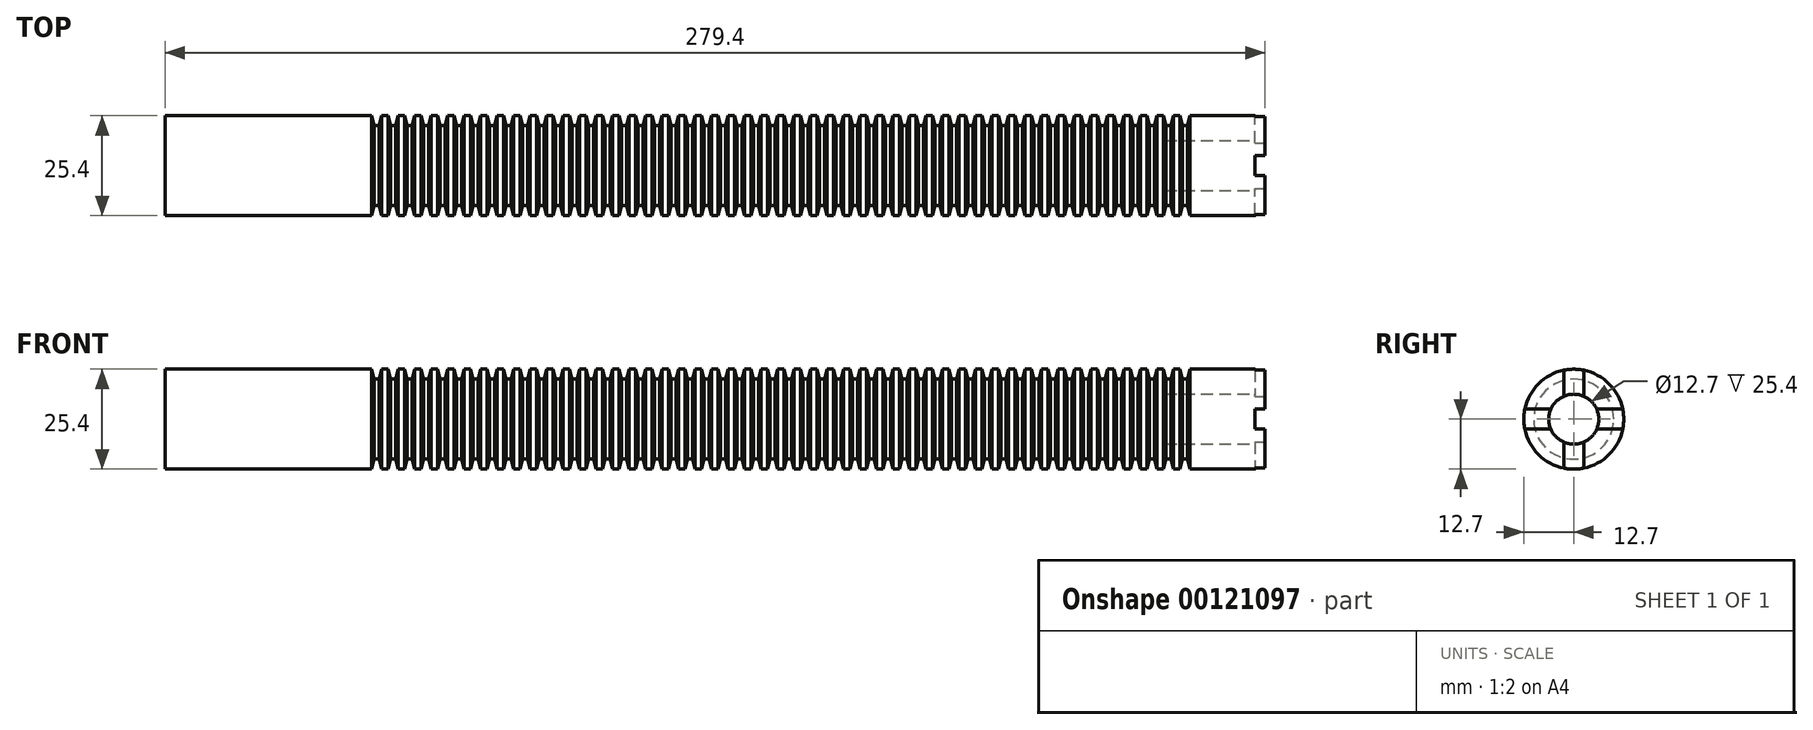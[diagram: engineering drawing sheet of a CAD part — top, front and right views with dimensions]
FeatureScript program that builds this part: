
annotation { "Feature Type Name" : "Feature", "Feature Type Description" : "" }
export const myFeature = defineFeature(function(context is Context, id is Id, definition is map)
    precondition{}
    {
        {
            var Q0;
            Q0=qCreatedBy(makeId("Front.planeOp"),FACE);
            var sketch = newSketch(context, id + "F0", { "sketchPlane" : qUnion([Q0])});
            skLineSegment(sketch, "E0.bottom", {"start": v(0, 0) * mm, "end": v(279.4, 0) * mm});
            skLineSegment(sketch, "E0.top", {"start": v(0, 12.7) * mm, "end": v(52.45, 12.7) * mm});
            skLineSegment(sketch, "E0.left", {"start": v(0, 0) * mm, "end": v(0, 12.7) * mm});
            skLineSegment(sketch, "E0.right", {"start": v(279.4, 0) * mm, "end": v(279.4, 12.7) * mm});
            skLineSegment(sketch, "E1", {"start": v(52.45, 12.7) * mm, "end": v(53.09, 10.16) * mm});
            skLineSegment(sketch, "E2", {"start": v(54.36, 10.16) * mm, "end": v(55, 12.7) * mm});
            skLineSegment(sketch, "E3", {"start": v(53.09, 10.16) * mm, "end": v(54.36, 10.16) * mm});
            skLineSegment(sketch, "E4.trimOffspring", {"start": v(55, 12.7) * mm, "end": v(56.64, 12.7) * mm});
            skLineSegment(sketch, "E5.1.0.0", {"start": v(56.64, 12.7) * mm, "end": v(57.28, 10.16) * mm});
            skLineSegment(sketch, "E5.1.0.1", {"start": v(58.55, 10.16) * mm, "end": v(59.18, 12.7) * mm});
            skLineSegment(sketch, "E5.1.0.2", {"start": v(57.28, 10.16) * mm, "end": v(58.55, 10.16) * mm});
            skLineSegment(sketch, "E5.2.0.0", {"start": v(60.83, 12.7) * mm, "end": v(61.47, 10.16) * mm});
            skLineSegment(sketch, "E5.2.0.1", {"start": v(62.74, 10.16) * mm, "end": v(63.37, 12.7) * mm});
            skLineSegment(sketch, "E5.2.0.2", {"start": v(61.47, 10.16) * mm, "end": v(62.74, 10.16) * mm});
            skLineSegment(sketch, "E5.direction1", {"start": v(55, 12.7) * mm, "end": v(56.64, 12.7) * mm, "construction": true});
            skLineSegment(sketch, "E6.0.3.0", {"start": v(65.02, 12.7) * mm, "end": v(65.66, 10.16) * mm});
            skLineSegment(sketch, "E6.3.3.0", {"start": v(66.93, 10.16) * mm, "end": v(67.56, 12.7) * mm});
            skLineSegment(sketch, "E6.6.3.0", {"start": v(65.66, 10.16) * mm, "end": v(66.93, 10.16) * mm});
            skLineSegment(sketch, "E6.0.4.0", {"start": v(69.21, 12.7) * mm, "end": v(69.85, 10.16) * mm});
            skLineSegment(sketch, "E6.3.4.0", {"start": v(71.12, 10.16) * mm, "end": v(71.75, 12.7) * mm});
            skLineSegment(sketch, "E6.6.4.0", {"start": v(69.85, 10.16) * mm, "end": v(71.12, 10.16) * mm});
            skLineSegment(sketch, "E6.0.5.0", {"start": v(73.4, 12.7) * mm, "end": v(74.04, 10.16) * mm});
            skLineSegment(sketch, "E6.3.5.0", {"start": v(75.31, 10.16) * mm, "end": v(75.95, 12.7) * mm});
            skLineSegment(sketch, "E6.6.5.0", {"start": v(74.04, 10.16) * mm, "end": v(75.31, 10.16) * mm});
            skLineSegment(sketch, "E6.0.6.0", {"start": v(77.6, 12.7) * mm, "end": v(78.23, 10.16) * mm});
            skLineSegment(sketch, "E6.3.6.0", {"start": v(79.5, 10.16) * mm, "end": v(80.14, 12.7) * mm});
            skLineSegment(sketch, "E6.6.6.0", {"start": v(78.23, 10.16) * mm, "end": v(79.5, 10.16) * mm});
            skLineSegment(sketch, "E6.0.7.0", {"start": v(81.79, 12.7) * mm, "end": v(82.42, 10.16) * mm});
            skLineSegment(sketch, "E6.3.7.0", {"start": v(83.7, 10.16) * mm, "end": v(84.33, 12.7) * mm});
            skLineSegment(sketch, "E6.6.7.0", {"start": v(82.42, 10.16) * mm, "end": v(83.7, 10.16) * mm});
            skLineSegment(sketch, "E6.0.8.0", {"start": v(85.98, 12.7) * mm, "end": v(86.61, 10.16) * mm});
            skLineSegment(sketch, "E6.3.8.0", {"start": v(87.88, 10.16) * mm, "end": v(88.52, 12.7) * mm});
            skLineSegment(sketch, "E6.6.8.0", {"start": v(86.61, 10.16) * mm, "end": v(87.88, 10.16) * mm});
            skLineSegment(sketch, "E6.0.9.0", {"start": v(90.17, 12.7) * mm, "end": v(90.8, 10.16) * mm});
            skLineSegment(sketch, "E6.3.9.0", {"start": v(92.07, 10.16) * mm, "end": v(92.7, 12.7) * mm});
            skLineSegment(sketch, "E6.6.9.0", {"start": v(90.8, 10.16) * mm, "end": v(92.07, 10.16) * mm});
            skLineSegment(sketch, "E6.0.10.0", {"start": v(94.36, 12.7) * mm, "end": v(95, 10.16) * mm});
            skLineSegment(sketch, "E6.3.10.0", {"start": v(96.27, 10.16) * mm, "end": v(96.9, 12.7) * mm});
            skLineSegment(sketch, "E6.6.10.0", {"start": v(95, 10.16) * mm, "end": v(96.27, 10.16) * mm});
            skLineSegment(sketch, "E6.0.11.0", {"start": v(98.55, 12.7) * mm, "end": v(99.19, 10.16) * mm});
            skLineSegment(sketch, "E6.3.11.0", {"start": v(100.46, 10.16) * mm, "end": v(101.1, 12.7) * mm});
            skLineSegment(sketch, "E6.6.11.0", {"start": v(99.19, 10.16) * mm, "end": v(100.46, 10.16) * mm});
            skLineSegment(sketch, "E6.0.12.0", {"start": v(102.74, 12.7) * mm, "end": v(103.38, 10.16) * mm});
            skLineSegment(sketch, "E6.3.12.0", {"start": v(104.65, 10.16) * mm, "end": v(105.28, 12.7) * mm});
            skLineSegment(sketch, "E6.6.12.0", {"start": v(103.38, 10.16) * mm, "end": v(104.65, 10.16) * mm});
            skLineSegment(sketch, "E6.0.13.0", {"start": v(106.93, 12.7) * mm, "end": v(107.57, 10.16) * mm});
            skLineSegment(sketch, "E6.3.13.0", {"start": v(108.84, 10.16) * mm, "end": v(109.47, 12.7) * mm});
            skLineSegment(sketch, "E6.6.13.0", {"start": v(107.57, 10.16) * mm, "end": v(108.84, 10.16) * mm});
            skLineSegment(sketch, "E6.0.14.0", {"start": v(111.12, 12.7) * mm, "end": v(111.76, 10.16) * mm});
            skLineSegment(sketch, "E6.3.14.0", {"start": v(113.03, 10.16) * mm, "end": v(113.66, 12.7) * mm});
            skLineSegment(sketch, "E6.6.14.0", {"start": v(111.76, 10.16) * mm, "end": v(113.03, 10.16) * mm});
            skLineSegment(sketch, "E6.0.15.0", {"start": v(115.32, 12.7) * mm, "end": v(115.95, 10.16) * mm});
            skLineSegment(sketch, "E6.3.15.0", {"start": v(117.22, 10.16) * mm, "end": v(117.86, 12.7) * mm});
            skLineSegment(sketch, "E6.6.15.0", {"start": v(115.95, 10.16) * mm, "end": v(117.22, 10.16) * mm});
            skLineSegment(sketch, "E6.0.16.0", {"start": v(119.5, 12.7) * mm, "end": v(120.14, 10.16) * mm});
            skLineSegment(sketch, "E6.3.16.0", {"start": v(121.41, 10.16) * mm, "end": v(122.05, 12.7) * mm});
            skLineSegment(sketch, "E6.6.16.0", {"start": v(120.14, 10.16) * mm, "end": v(121.41, 10.16) * mm});
            skLineSegment(sketch, "E6.0.17.0", {"start": v(123.7, 12.7) * mm, "end": v(124.33, 10.16) * mm});
            skLineSegment(sketch, "E6.3.17.0", {"start": v(125.6, 10.16) * mm, "end": v(126.24, 12.7) * mm});
            skLineSegment(sketch, "E6.6.17.0", {"start": v(124.33, 10.16) * mm, "end": v(125.6, 10.16) * mm});
            skLineSegment(sketch, "E6.0.18.0", {"start": v(127.89, 12.7) * mm, "end": v(128.52, 10.16) * mm});
            skLineSegment(sketch, "E6.3.18.0", {"start": v(129.8, 10.16) * mm, "end": v(130.43, 12.7) * mm});
            skLineSegment(sketch, "E6.6.18.0", {"start": v(128.52, 10.16) * mm, "end": v(129.8, 10.16) * mm});
            skLineSegment(sketch, "E6.0.19.0", {"start": v(132.08, 12.7) * mm, "end": v(132.72, 10.16) * mm});
            skLineSegment(sketch, "E6.3.19.0", {"start": v(133.98, 10.16) * mm, "end": v(134.62, 12.7) * mm});
            skLineSegment(sketch, "E6.6.19.0", {"start": v(132.72, 10.16) * mm, "end": v(133.98, 10.16) * mm});
            skLineSegment(sketch, "E6.0.20.0", {"start": v(136.27, 12.7) * mm, "end": v(136.9, 10.16) * mm});
            skLineSegment(sketch, "E6.3.20.0", {"start": v(138.18, 10.16) * mm, "end": v(138.81, 12.7) * mm});
            skLineSegment(sketch, "E6.6.20.0", {"start": v(136.9, 10.16) * mm, "end": v(138.18, 10.16) * mm});
            skLineSegment(sketch, "E6.0.21.0", {"start": v(140.46, 12.7) * mm, "end": v(141.1, 10.16) * mm});
            skLineSegment(sketch, "E6.3.21.0", {"start": v(142.37, 10.16) * mm, "end": v(143, 12.7) * mm});
            skLineSegment(sketch, "E6.6.21.0", {"start": v(141.1, 10.16) * mm, "end": v(142.37, 10.16) * mm});
            skLineSegment(sketch, "E6.0.22.0", {"start": v(144.65, 12.7) * mm, "end": v(145.29, 10.16) * mm});
            skLineSegment(sketch, "E6.3.22.0", {"start": v(146.56, 10.16) * mm, "end": v(147.2, 12.7) * mm});
            skLineSegment(sketch, "E6.6.22.0", {"start": v(145.29, 10.16) * mm, "end": v(146.56, 10.16) * mm});
            skLineSegment(sketch, "E6.0.23.0", {"start": v(148.84, 12.7) * mm, "end": v(149.48, 10.16) * mm});
            skLineSegment(sketch, "E6.3.23.0", {"start": v(150.75, 10.16) * mm, "end": v(151.38, 12.7) * mm});
            skLineSegment(sketch, "E6.6.23.0", {"start": v(149.48, 10.16) * mm, "end": v(150.75, 10.16) * mm});
            skLineSegment(sketch, "E6.0.24.0", {"start": v(153.03, 12.7) * mm, "end": v(153.67, 10.16) * mm});
            skLineSegment(sketch, "E6.3.24.0", {"start": v(154.94, 10.16) * mm, "end": v(155.57, 12.7) * mm});
            skLineSegment(sketch, "E6.6.24.0", {"start": v(153.67, 10.16) * mm, "end": v(154.94, 10.16) * mm});
            skLineSegment(sketch, "E6.0.25.0", {"start": v(157.23, 12.7) * mm, "end": v(157.86, 10.16) * mm});
            skLineSegment(sketch, "E6.3.25.0", {"start": v(159.13, 10.16) * mm, "end": v(159.77, 12.7) * mm});
            skLineSegment(sketch, "E6.6.25.0", {"start": v(157.86, 10.16) * mm, "end": v(159.13, 10.16) * mm});
            skLineSegment(sketch, "E6.0.26.0", {"start": v(161.42, 12.7) * mm, "end": v(162.05, 10.16) * mm});
            skLineSegment(sketch, "E6.3.26.0", {"start": v(163.32, 10.16) * mm, "end": v(163.96, 12.7) * mm});
            skLineSegment(sketch, "E6.6.26.0", {"start": v(162.05, 10.16) * mm, "end": v(163.32, 10.16) * mm});
            skLineSegment(sketch, "E6.0.27.0", {"start": v(165.6, 12.7) * mm, "end": v(166.24, 10.16) * mm});
            skLineSegment(sketch, "E6.3.27.0", {"start": v(167.51, 10.16) * mm, "end": v(168.15, 12.7) * mm});
            skLineSegment(sketch, "E6.6.27.0", {"start": v(166.24, 10.16) * mm, "end": v(167.51, 10.16) * mm});
            skLineSegment(sketch, "E6.0.28.0", {"start": v(169.8, 12.7) * mm, "end": v(170.43, 10.16) * mm});
            skLineSegment(sketch, "E6.3.28.0", {"start": v(171.7, 10.16) * mm, "end": v(172.34, 12.7) * mm});
            skLineSegment(sketch, "E6.6.28.0", {"start": v(170.43, 10.16) * mm, "end": v(171.7, 10.16) * mm});
            skLineSegment(sketch, "E6.0.29.0", {"start": v(173.99, 12.7) * mm, "end": v(174.63, 10.16) * mm});
            skLineSegment(sketch, "E6.3.29.0", {"start": v(175.9, 10.16) * mm, "end": v(176.53, 12.7) * mm});
            skLineSegment(sketch, "E6.6.29.0", {"start": v(174.63, 10.16) * mm, "end": v(175.9, 10.16) * mm});
            skLineSegment(sketch, "E6.0.30.0", {"start": v(178.18, 12.7) * mm, "end": v(178.82, 10.16) * mm});
            skLineSegment(sketch, "E6.3.30.0", {"start": v(180.09, 10.16) * mm, "end": v(180.72, 12.7) * mm});
            skLineSegment(sketch, "E6.6.30.0", {"start": v(178.82, 10.16) * mm, "end": v(180.09, 10.16) * mm});
            skLineSegment(sketch, "E6.0.31.0", {"start": v(182.37, 12.7) * mm, "end": v(183, 10.16) * mm});
            skLineSegment(sketch, "E6.3.31.0", {"start": v(184.28, 10.16) * mm, "end": v(184.91, 12.7) * mm});
            skLineSegment(sketch, "E6.6.31.0", {"start": v(183, 10.16) * mm, "end": v(184.28, 10.16) * mm});
            skLineSegment(sketch, "E6.0.32.0", {"start": v(186.56, 12.7) * mm, "end": v(187.2, 10.16) * mm});
            skLineSegment(sketch, "E6.3.32.0", {"start": v(188.47, 10.16) * mm, "end": v(189.1, 12.7) * mm});
            skLineSegment(sketch, "E6.6.32.0", {"start": v(187.2, 10.16) * mm, "end": v(188.47, 10.16) * mm});
            skLineSegment(sketch, "E6.0.33.0", {"start": v(190.75, 12.7) * mm, "end": v(191.39, 10.16) * mm});
            skLineSegment(sketch, "E6.3.33.0", {"start": v(192.66, 10.16) * mm, "end": v(193.3, 12.7) * mm});
            skLineSegment(sketch, "E6.6.33.0", {"start": v(191.39, 10.16) * mm, "end": v(192.66, 10.16) * mm});
            skLineSegment(sketch, "E6.0.34.0", {"start": v(194.94, 12.7) * mm, "end": v(195.58, 10.16) * mm});
            skLineSegment(sketch, "E6.3.34.0", {"start": v(196.85, 10.16) * mm, "end": v(197.48, 12.7) * mm});
            skLineSegment(sketch, "E6.6.34.0", {"start": v(195.58, 10.16) * mm, "end": v(196.85, 10.16) * mm});
            skLineSegment(sketch, "E6.0.35.0", {"start": v(199.14, 12.7) * mm, "end": v(199.77, 10.16) * mm});
            skLineSegment(sketch, "E6.3.35.0", {"start": v(201.04, 10.16) * mm, "end": v(201.68, 12.7) * mm});
            skLineSegment(sketch, "E6.6.35.0", {"start": v(199.77, 10.16) * mm, "end": v(201.04, 10.16) * mm});
            skLineSegment(sketch, "E6.0.36.0", {"start": v(203.33, 12.7) * mm, "end": v(203.96, 10.16) * mm});
            skLineSegment(sketch, "E6.3.36.0", {"start": v(205.23, 10.16) * mm, "end": v(205.87, 12.7) * mm});
            skLineSegment(sketch, "E6.6.36.0", {"start": v(203.96, 10.16) * mm, "end": v(205.23, 10.16) * mm});
            skLineSegment(sketch, "E6.0.37.0", {"start": v(207.52, 12.7) * mm, "end": v(208.15, 10.16) * mm});
            skLineSegment(sketch, "E6.3.37.0", {"start": v(209.42, 10.16) * mm, "end": v(210.06, 12.7) * mm});
            skLineSegment(sketch, "E6.6.37.0", {"start": v(208.15, 10.16) * mm, "end": v(209.42, 10.16) * mm});
            skLineSegment(sketch, "E6.0.38.0", {"start": v(211.7, 12.7) * mm, "end": v(212.34, 10.16) * mm});
            skLineSegment(sketch, "E6.3.38.0", {"start": v(213.61, 10.16) * mm, "end": v(214.25, 12.7) * mm});
            skLineSegment(sketch, "E6.6.38.0", {"start": v(212.34, 10.16) * mm, "end": v(213.61, 10.16) * mm});
            skLineSegment(sketch, "E6.0.39.0", {"start": v(215.9, 12.7) * mm, "end": v(216.54, 10.16) * mm});
            skLineSegment(sketch, "E6.3.39.0", {"start": v(217.8, 10.16) * mm, "end": v(218.44, 12.7) * mm});
            skLineSegment(sketch, "E6.6.39.0", {"start": v(216.54, 10.16) * mm, "end": v(217.8, 10.16) * mm});
            skLineSegment(sketch, "E6.0.40.0", {"start": v(220.1, 12.7) * mm, "end": v(220.73, 10.16) * mm});
            skLineSegment(sketch, "E6.3.40.0", {"start": v(222, 10.16) * mm, "end": v(222.63, 12.7) * mm});
            skLineSegment(sketch, "E6.6.40.0", {"start": v(220.73, 10.16) * mm, "end": v(222, 10.16) * mm});
            skLineSegment(sketch, "E6.0.41.0", {"start": v(224.28, 12.7) * mm, "end": v(224.92, 10.16) * mm});
            skLineSegment(sketch, "E6.3.41.0", {"start": v(226.19, 10.16) * mm, "end": v(226.82, 12.7) * mm});
            skLineSegment(sketch, "E6.6.41.0", {"start": v(224.92, 10.16) * mm, "end": v(226.19, 10.16) * mm});
            skLineSegment(sketch, "E6.0.42.0", {"start": v(228.47, 12.7) * mm, "end": v(229.1, 10.16) * mm});
            skLineSegment(sketch, "E6.3.42.0", {"start": v(230.38, 10.16) * mm, "end": v(231.01, 12.7) * mm});
            skLineSegment(sketch, "E6.6.42.0", {"start": v(229.1, 10.16) * mm, "end": v(230.38, 10.16) * mm});
            skLineSegment(sketch, "E6.0.43.0", {"start": v(232.66, 12.7) * mm, "end": v(233.3, 10.16) * mm});
            skLineSegment(sketch, "E6.3.43.0", {"start": v(234.57, 10.16) * mm, "end": v(235.2, 12.7) * mm});
            skLineSegment(sketch, "E6.6.43.0", {"start": v(233.3, 10.16) * mm, "end": v(234.57, 10.16) * mm});
            skLineSegment(sketch, "E6.0.44.0", {"start": v(236.85, 12.7) * mm, "end": v(237.5, 10.16) * mm});
            skLineSegment(sketch, "E6.3.44.0", {"start": v(238.76, 10.16) * mm, "end": v(239.4, 12.7) * mm});
            skLineSegment(sketch, "E6.6.44.0", {"start": v(237.5, 10.16) * mm, "end": v(238.76, 10.16) * mm});
            skLineSegment(sketch, "E6.0.45.0", {"start": v(241.05, 12.7) * mm, "end": v(241.68, 10.16) * mm});
            skLineSegment(sketch, "E6.3.45.0", {"start": v(242.95, 10.16) * mm, "end": v(243.59, 12.7) * mm});
            skLineSegment(sketch, "E6.6.45.0", {"start": v(241.68, 10.16) * mm, "end": v(242.95, 10.16) * mm});
            skLineSegment(sketch, "E6.0.46.0", {"start": v(245.24, 12.7) * mm, "end": v(245.87, 10.16) * mm});
            skLineSegment(sketch, "E6.3.46.0", {"start": v(247.14, 10.16) * mm, "end": v(247.78, 12.7) * mm});
            skLineSegment(sketch, "E6.6.46.0", {"start": v(245.87, 10.16) * mm, "end": v(247.14, 10.16) * mm});
            skLineSegment(sketch, "E6.0.47.0", {"start": v(249.43, 12.7) * mm, "end": v(250.06, 10.16) * mm});
            skLineSegment(sketch, "E6.3.47.0", {"start": v(251.33, 10.16) * mm, "end": v(251.97, 12.7) * mm});
            skLineSegment(sketch, "E6.6.47.0", {"start": v(250.06, 10.16) * mm, "end": v(251.33, 10.16) * mm});
            skLineSegment(sketch, "E6.0.48.0", {"start": v(253.62, 12.7) * mm, "end": v(254.25, 10.16) * mm});
            skLineSegment(sketch, "E6.3.48.0", {"start": v(255.52, 10.16) * mm, "end": v(256.16, 12.7) * mm});
            skLineSegment(sketch, "E6.6.48.0", {"start": v(254.25, 10.16) * mm, "end": v(255.52, 10.16) * mm});
            skLineSegment(sketch, "E6.0.49.0", {"start": v(257.8, 12.7) * mm, "end": v(258.45, 10.16) * mm});
            skLineSegment(sketch, "E6.3.49.0", {"start": v(259.71, 10.16) * mm, "end": v(260.35, 12.7) * mm});
            skLineSegment(sketch, "E6.6.49.0", {"start": v(258.45, 10.16) * mm, "end": v(259.71, 10.16) * mm});
            skLineSegment(sketch, "E7.trimOffspring", {"start": v(260.35, 12.7) * mm, "end": v(279.4, 12.7) * mm});
            skLineSegment(sketch, "E8.trimOffspring", {"start": v(256.16, 12.7) * mm, "end": v(257.8, 12.7) * mm});
            skLineSegment(sketch, "E9.trimOffspring", {"start": v(251.97, 12.7) * mm, "end": v(253.62, 12.7) * mm});
            skLineSegment(sketch, "E10.trimOffspring", {"start": v(247.78, 12.7) * mm, "end": v(249.43, 12.7) * mm});
            skLineSegment(sketch, "E11.trimOffspring", {"start": v(243.59, 12.7) * mm, "end": v(245.24, 12.7) * mm});
            skLineSegment(sketch, "E12.trimOffspring", {"start": v(239.4, 12.7) * mm, "end": v(241.05, 12.7) * mm});
            skLineSegment(sketch, "E13.trimOffspring", {"start": v(235.2, 12.7) * mm, "end": v(236.86, 12.7) * mm});
            skLineSegment(sketch, "E14.trimOffspring", {"start": v(231.01, 12.7) * mm, "end": v(232.66, 12.7) * mm});
            skLineSegment(sketch, "E15.trimOffspring", {"start": v(226.82, 12.7) * mm, "end": v(228.47, 12.7) * mm});
            skLineSegment(sketch, "E16.trimOffspring", {"start": v(222.63, 12.7) * mm, "end": v(224.28, 12.7) * mm});
            skLineSegment(sketch, "E17.trimOffspring", {"start": v(218.44, 12.7) * mm, "end": v(220.1, 12.7) * mm});
            skLineSegment(sketch, "E18.trimOffspring", {"start": v(214.25, 12.7) * mm, "end": v(215.9, 12.7) * mm});
            skLineSegment(sketch, "E19.trimOffspring", {"start": v(210.06, 12.7) * mm, "end": v(211.7, 12.7) * mm});
            skLineSegment(sketch, "E20.trimOffspring", {"start": v(205.87, 12.7) * mm, "end": v(207.52, 12.7) * mm});
            skLineSegment(sketch, "E21.trimOffspring", {"start": v(201.68, 12.7) * mm, "end": v(203.33, 12.7) * mm});
            skLineSegment(sketch, "E22.trimOffspring", {"start": v(197.49, 12.7) * mm, "end": v(199.14, 12.7) * mm});
            skLineSegment(sketch, "E23.trimOffspring", {"start": v(193.3, 12.7) * mm, "end": v(194.94, 12.7) * mm});
            skLineSegment(sketch, "E24.trimOffspring", {"start": v(189.1, 12.7) * mm, "end": v(190.75, 12.7) * mm});
            skLineSegment(sketch, "E25.trimOffspring", {"start": v(184.91, 12.7) * mm, "end": v(186.56, 12.7) * mm});
            skLineSegment(sketch, "E26.trimOffspring", {"start": v(180.72, 12.7) * mm, "end": v(182.37, 12.7) * mm});
            skLineSegment(sketch, "E27.trimOffspring", {"start": v(172.34, 12.7) * mm, "end": v(174, 12.7) * mm});
            skLineSegment(sketch, "E28.trimOffspring", {"start": v(168.15, 12.7) * mm, "end": v(169.8, 12.7) * mm});
            skLineSegment(sketch, "E29.trimOffspring", {"start": v(163.96, 12.7) * mm, "end": v(165.6, 12.7) * mm});
            skLineSegment(sketch, "E30.trimOffspring", {"start": v(159.77, 12.7) * mm, "end": v(161.42, 12.7) * mm});
            skLineSegment(sketch, "E31.trimOffspring", {"start": v(155.58, 12.7) * mm, "end": v(157.23, 12.7) * mm});
            skLineSegment(sketch, "E32.trimOffspring", {"start": v(151.38, 12.7) * mm, "end": v(153.03, 12.7) * mm});
            skLineSegment(sketch, "E33.trimOffspring", {"start": v(147.2, 12.7) * mm, "end": v(148.84, 12.7) * mm});
            skLineSegment(sketch, "E34.trimOffspring", {"start": v(143, 12.7) * mm, "end": v(144.65, 12.7) * mm});
            skLineSegment(sketch, "E35.trimOffspring", {"start": v(138.81, 12.7) * mm, "end": v(140.46, 12.7) * mm});
            skLineSegment(sketch, "E36.trimOffspring", {"start": v(134.62, 12.7) * mm, "end": v(136.27, 12.7) * mm});
            skLineSegment(sketch, "E37.trimOffspring", {"start": v(130.43, 12.7) * mm, "end": v(132.08, 12.7) * mm});
            skLineSegment(sketch, "E38.trimOffspring", {"start": v(126.24, 12.7) * mm, "end": v(127.89, 12.7) * mm});
            skLineSegment(sketch, "E39.trimOffspring", {"start": v(122.05, 12.7) * mm, "end": v(123.7, 12.7) * mm});
            skLineSegment(sketch, "E40.trimOffspring", {"start": v(117.86, 12.7) * mm, "end": v(119.5, 12.7) * mm});
            skLineSegment(sketch, "E41.trimOffspring", {"start": v(113.67, 12.7) * mm, "end": v(115.32, 12.7) * mm});
            skLineSegment(sketch, "E42.trimOffspring", {"start": v(109.47, 12.7) * mm, "end": v(111.12, 12.7) * mm});
            skLineSegment(sketch, "E43.trimOffspring", {"start": v(105.28, 12.7) * mm, "end": v(106.93, 12.7) * mm});
            skLineSegment(sketch, "E44.trimOffspring", {"start": v(101.1, 12.7) * mm, "end": v(102.74, 12.7) * mm});
            skLineSegment(sketch, "E45.trimOffspring", {"start": v(96.9, 12.7) * mm, "end": v(98.55, 12.7) * mm});
            skLineSegment(sketch, "E46.trimOffspring", {"start": v(92.71, 12.7) * mm, "end": v(94.36, 12.7) * mm});
            skLineSegment(sketch, "E47.trimOffspring", {"start": v(88.52, 12.7) * mm, "end": v(90.17, 12.7) * mm});
            skLineSegment(sketch, "E48.trimOffspring", {"start": v(84.33, 12.7) * mm, "end": v(85.98, 12.7) * mm});
            skLineSegment(sketch, "E49.trimOffspring", {"start": v(80.14, 12.7) * mm, "end": v(81.79, 12.7) * mm});
            skLineSegment(sketch, "E50.trimOffspring", {"start": v(75.95, 12.7) * mm, "end": v(77.6, 12.7) * mm});
            skLineSegment(sketch, "E51.trimOffspring", {"start": v(71.76, 12.7) * mm, "end": v(73.4, 12.7) * mm});
            skLineSegment(sketch, "E52.trimOffspring", {"start": v(67.56, 12.7) * mm, "end": v(69.21, 12.7) * mm});
            skLineSegment(sketch, "E53.trimOffspring", {"start": v(63.37, 12.7) * mm, "end": v(65.02, 12.7) * mm});
            skLineSegment(sketch, "E54.trimOffspring", {"start": v(59.18, 12.7) * mm, "end": v(60.83, 12.7) * mm});
            skLineSegment(sketch, "E55", {"start": v(176.53, 12.7) * mm, "end": v(178.18, 12.7) * mm});
            skSolve(sketch);
        }
        {
            var Q0;
            Q0=makeQuery(id+"F0.imprint","IMPRINT",FACE,{"disambiguationData":[TD([[makeQuery(id+"F0.imprint","IMPRINT",EDGE,{"derivedFrom":sQuery(id+"F0.wireOp",EDGE,"E0.bottom")}),1.0]])]});
            var Q1;
            Q1=sQuery(id+"F0.wireOp",EDGE,"E0.bottom");
            revolve(context, id + "F1", {"entities" : qUnion([Q0]), "axis" : qUnion([Q1]), "revolveType" : RevolveType.FULL});
        }
        {
            var Q0;
            Q0=makeQuery(id+"F1.opRevolve","SWEPT_FACE",FACE,{"disambiguationData":[OSD([sQuery(id+"F0.wireOp",EDGE,"E0.right")])]});
            var sketch = newSketch(context, id + "F2", { "sketchPlane" : qUnion([Q0])});
            skCircle(sketch, "E56", {"center": v(0, 0) * mm, "radius": 6.35 * mm});
            skSolve(sketch);
        }
        {
            var Q0;
            Q0 = qSketchRegion(id + "F2", true);
            extrude(context, id + "F3", {"entities" : qUnion([Q0]), "operationType" : NewBodyOperationType.REMOVE, "oppositeDirection" : true, "depth" : 25.4 * mm});
        }
        {
            var Q0;
            Q0=makeQuery(id+"F1.opRevolve","SWEPT_FACE",FACE,{"disambiguationData":[OSD([sQuery(id+"F0.wireOp",EDGE,"E0.right")])]});
            var sketch = newSketch(context, id + "F4", { "sketchPlane" : qUnion([Q0])});
            skLineSegment(sketch, "E57.bottom", {"start": v(-2.54, 12.7) * mm, "end": v(2.54, 12.7) * mm});
            skLineSegment(sketch, "E57.top", {"start": v(-2.54, -12.7) * mm, "end": v(2.54, -12.7) * mm});
            skLineSegment(sketch, "E57.left", {"start": v(-2.54, 12.7) * mm, "end": v(-2.54, -12.7) * mm});
            skLineSegment(sketch, "E57.right", {"start": v(2.54, 12.7) * mm, "end": v(2.54, -12.7) * mm});
            skLineSegment(sketch, "E58.bottom", {"start": v(-12.7, 2.54) * mm, "end": v(12.7, 2.54) * mm});
            skLineSegment(sketch, "E58.top", {"start": v(-12.7, -2.54) * mm, "end": v(12.7, -2.54) * mm});
            skLineSegment(sketch, "E58.left", {"start": v(-12.7, 2.54) * mm, "end": v(-12.7, -2.54) * mm});
            skLineSegment(sketch, "E58.right", {"start": v(12.7, 2.54) * mm, "end": v(12.7, -2.54) * mm});
            skSolve(sketch);
        }
        {
            var Q0;
            Q0 = qSketchRegion(id + "F4", true);
            extrude(context, id + "F5", {"entities" : qUnion([Q0]), "operationType" : NewBodyOperationType.REMOVE, "oppositeDirection" : true, "depth" : 2.54 * mm});
        }
    });
